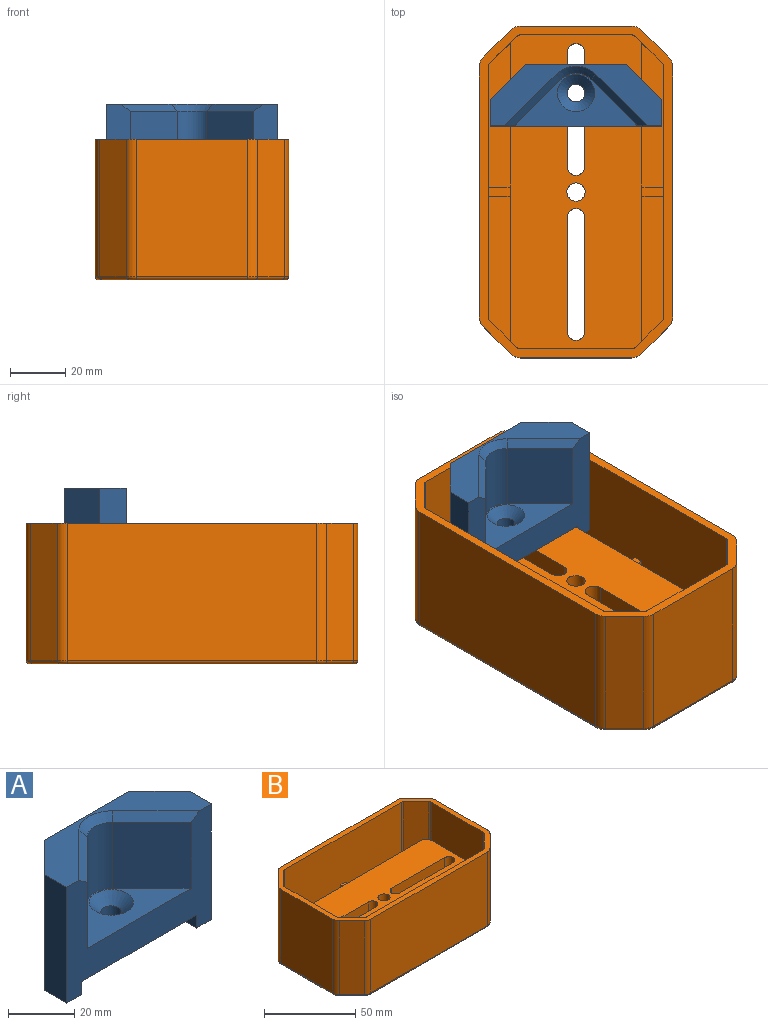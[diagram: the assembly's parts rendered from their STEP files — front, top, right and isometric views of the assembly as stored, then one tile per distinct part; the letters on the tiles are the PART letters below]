
ASSEMBLY  parts=2 mates=1
PART A: 21 faces, bbox 61.9x22.2x42.9 mm
  f0: plane 61.91x42.86mm, normal (0,-1,0), area 1210.6mm2, adj f1,f2,f5,f6,f7,f9,f10,f11
  f1: plane 61.91x22.23mm, normal (0,0,1), area 570.5mm2, adj f0,f3,f4,f5,f7,f8,f16,f17
  f2: plane 15.88x6.35mm, normal (0,0,-1), area 80.6mm2, adj f0,f7,f8,f10
  f3: plane 38.1x36.51mm, normal (0,1,0), area 1391.1mm2, adj f1,f4,f8,f11
  f4: plane 42.86x12.7mm, normal (-0.71,0.71,0), area 727.1mm2, adj f1,f3,f5,f6,f9,f11
  f5: plane 42.86x9.53mm, normal (-1,0,0), area 408.3mm2, adj f0,f1,f4,f6
  f6: plane 15.88x6.35mm, normal (0,0,-1), area 80.6mm2, adj f0,f4,f5,f9
  f7: plane 42.86x9.53mm, normal (1,0,0), area 408.3mm2, adj f0,f1,f2,f8
  f8: plane 42.86x12.7mm, normal (0.71,0.71,0), area 727.1mm2, adj f1,f2,f3,f7,f10,f11
  f9: plane 15.88x4.76mm, normal (1,0,0), area 75.6mm2, adj f0,f4,f6,f11
  f10: plane 15.88x4.76mm, normal (-1,0,0), area 75.6mm2, adj f0,f2,f8,f11
  f11: plane 49.21x22.23mm, normal (0,0,-1), area 1021.3mm2, adj f0,f3,f4,f8,f9,f10,f19
  f12: plane 24.45x16.81mm, normal (0.71,-0.71,0), area 581mm2, adj f0,f14,f15,f16
  f13: plane 24.45x16.81mm, normal (-0.71,-0.71,0), area 581mm2, adj f0,f14,f15,f18
  f14: cylinder r=7.67mm len=24.45mm, axis (0,0,1), area 294.4mm2, adj f12,f13,f15,f17
  f15: plane 44.45x19.05mm, normal (0,0,1), area 339.5mm2, adj f0,f12,f13,f14,f20
  f16: plane 20.4x18.6mm, normal (0.5,-0.5,0.71), area 89.9mm2, adj f0,f1,f12,f17
  f17: cone r=7.67mm half-angle=45deg, axis (0,0,1), area 50.4mm2, adj f1,f14,f16,f18
  f18: plane 20.4x18.6mm, normal (-0.5,-0.5,0.71), area 89.9mm2, adj f0,f1,f13,f17
  f19: cylinder r=3.2mm len=7.59mm, axis (0,0,1), area 152.7mm2, adj f11,f20
  f20: cone r=3.2mm half-angle=45deg, axis (0,0,1), area 155.1mm2, adj f15,f19
PART B: 81 faces, bbox 120.7x70.7x50.8 mm
  f0: plane 113.54x47.63mm, normal (0,0,1), area 4768.3mm2, adj f18,f20,f22,f23,f24,f25,f28,f29
  f1: plane 49.53x40.24mm, normal (-1,0,0), area 1993.2mm2, adj f5,f16,f17,f35
  f2: plane 90.28x49.53mm, normal (0,-1,0), area 4471.5mm2, adj f5,f10,f11,f42
  f3: plane 49.53x40.24mm, normal (1,0,0), area 1993.2mm2, adj f5,f12,f13,f50
  f4: plane 90.28x49.53mm, normal (0,1,0), area 4471.5mm2, adj f5,f14,f15,f43
  f5: plane 119.89x69.85mm, normal (0,0,1), area 1073.1mm2, adj f1,f2,f3,f4,f6,f7,f8,f9
  f6: plane 49.53x9.72mm, normal (-0.71,0.71,0), area 681.1mm2, adj f5,f14,f16,f39
  f7: plane 49.53x9.72mm, normal (0.71,0.71,0), area 681.1mm2, adj f5,f12,f15,f47
  f8: plane 49.53x9.72mm, normal (0.71,-0.71,0), area 681.1mm2, adj f5,f10,f13,f46
  f9: plane 49.53x9.72mm, normal (-0.71,-0.71,0), area 681.1mm2, adj f5,f11,f17,f38
  f10: cylinder r=5.08mm len=49.53mm, axis (0,0,1), area 197.6mm2, adj f2,f5,f8,f44
  f11: cylinder r=5.08mm len=49.53mm, axis (0,0,1), area 197.6mm2, adj f2,f5,f9,f40
  f12: cylinder r=5.08mm len=49.53mm, axis (0,0,-1), area 197.6mm2, adj f3,f5,f7,f49
  f13: cylinder r=5.08mm len=49.53mm, axis (0,0,-1), area 197.6mm2, adj f3,f5,f8,f48
  f14: cylinder r=5.08mm len=49.53mm, axis (0,0,-1), area 197.6mm2, adj f4,f5,f6,f41
  f15: cylinder r=5.08mm len=49.53mm, axis (0,0,-1), area 197.6mm2, adj f4,f5,f7,f45
  f16: cylinder r=5.08mm len=49.53mm, axis (0,0,1), area 197.6mm2, adj f1,f5,f6,f37
  f17: cylinder r=5.08mm len=49.53mm, axis (0,0,1), area 197.6mm2, adj f1,f5,f9,f36
  f18: plane 40.24x25.4mm, normal (1,0,0), area 1022.1mm2, adj f0,f5,f32,f33
  f19: plane 90.28x47.63mm, normal (0,1,0), area 4249.2mm2, adj f5,f26,f27,f74,f75,f76,f77,f79
  f20: plane 40.24x25.4mm, normal (-1,0,0), area 1022.1mm2, adj f0,f5,f28,f29
  f21: plane 90.28x47.63mm, normal (0,-1,0), area 4249.2mm2, adj f5,f30,f31,f69,f70,f71,f72,f80
  f22: plane 47.63x9.72mm, normal (0.71,-0.71,0), area 581.2mm2, adj f0,f5,f30,f32,f69,f73
  f23: plane 47.63x9.72mm, normal (-0.71,-0.71,0), area 581.2mm2, adj f0,f5,f28,f31,f71,f73
  f24: plane 47.63x9.72mm, normal (-0.71,0.71,0), area 581.2mm2, adj f0,f5,f26,f29,f74,f78
  f25: plane 47.63x9.72mm, normal (0.71,0.71,0), area 581.2mm2, adj f0,f5,f27,f33,f76,f78
  f26: cylinder r=1.91mm len=47.63mm, axis (0,0,1), area 71.3mm2, adj f5,f19,f24,f74
  f27: cylinder r=1.91mm len=47.63mm, axis (0,0,1), area 71.3mm2, adj f5,f19,f25,f76
  f28: cylinder r=1.91mm len=25.4mm, axis (0,0,-1), area 38mm2, adj f0,f5,f20,f23
  f29: cylinder r=1.91mm len=25.4mm, axis (0,0,-1), area 38mm2, adj f0,f5,f20,f24
  f30: cylinder r=1.91mm len=47.63mm, axis (0,0,-1), area 71.3mm2, adj f5,f21,f22,f69
  f31: cylinder r=1.91mm len=47.63mm, axis (0,0,-1), area 71.3mm2, adj f5,f21,f23,f71
  f32: cylinder r=1.91mm len=25.4mm, axis (0,0,1), area 38mm2, adj f0,f5,f18,f22
  f33: cylinder r=1.91mm len=25.4mm, axis (0,0,1), area 38mm2, adj f0,f5,f18,f25
  f34: plane 117.35x67.31mm, normal (0,0,-1), area 3293.2mm2, adj f35,f36,f37,f38,f39,f40,f41,f42
  f35: cylinder r=1.27mm len=40.24mm, axis (0,-1,0), area 80.3mm2, adj f1,f34,f36,f37
  f36: torus R=3.81mm, axis (0,0,1), area 7.2mm2, adj f17,f34,f35,f38
  f37: torus R=3.81mm, axis (0,0,1), area 7.2mm2, adj f16,f34,f35,f39
  f38: cylinder r=1.27mm len=10.62mm, axis (0.71,-0.71,0), area 27.4mm2, adj f9,f34,f36,f40
  f39: cylinder r=1.27mm len=10.62mm, axis (0.71,0.71,0), area 27.4mm2, adj f6,f34,f37,f41
  f40: torus R=3.81mm, axis (0,0,1), area 7.2mm2, adj f11,f34,f38,f42
  f41: torus R=3.81mm, axis (0,0,1), area 7.2mm2, adj f14,f34,f39,f43
  f42: cylinder r=1.27mm len=90.28mm, axis (1,0,0), area 180.1mm2, adj f2,f34,f40,f44
  f43: cylinder r=1.27mm len=90.28mm, axis (-1,0,0), area 180.1mm2, adj f4,f34,f41,f45
  f44: torus R=3.81mm, axis (0,0,1), area 7.2mm2, adj f10,f34,f42,f46
  f45: torus R=3.81mm, axis (0,0,1), area 7.2mm2, adj f15,f34,f43,f47
  f46: cylinder r=1.27mm len=10.62mm, axis (-0.71,-0.71,0), area 27.4mm2, adj f8,f34,f44,f48
  f47: cylinder r=1.27mm len=10.62mm, axis (-0.71,0.71,0), area 27.4mm2, adj f7,f34,f45,f49
  f48: torus R=3.81mm, axis (0,0,1), area 7.2mm2, adj f13,f34,f46,f50
  f49: torus R=3.81mm, axis (0,0,1), area 7.2mm2, adj f12,f34,f47,f50
  f50: cylinder r=1.27mm len=40.24mm, axis (0,1,0), area 80.3mm2, adj f3,f34,f48,f49
  f51: plane 31.75x12.7mm, normal (1,0,0), area 403.2mm2, adj f34,f52,f58,f59
  f52: cylinder r=3.17mm len=12.7mm, axis (0,0,-1), area 63.3mm2, adj f34,f51,f53,f59
  f53: plane 107.19x12.7mm, normal (0,-1,0), area 1361.3mm2, adj f34,f52,f54,f59
  f54: cylinder r=3.17mm len=12.7mm, axis (0,0,-1), area 63.3mm2, adj f34,f53,f55,f59
  f55: plane 31.75x12.7mm, normal (-1,0,0), area 403.2mm2, adj f34,f54,f56,f59
  f56: cylinder r=3.17mm len=12.7mm, axis (0,0,-1), area 63.3mm2, adj f34,f55,f57,f59
  f57: plane 107.19x12.7mm, normal (0,1,0), area 1361.3mm2, adj f34,f56,f58,f59
  f58: cylinder r=3.17mm len=12.7mm, axis (0,0,-1), area 63.3mm2, adj f34,f51,f57,f59
  f59: plane 113.54x38.1mm, normal (0,0,-1), area 3695.4mm2, adj f51,f52,f53,f54,f55,f56,f57,f58
  f60: cylinder r=3.3mm len=12.7mm, axis (0,0,1), area 263.3mm2, adj f0,f59
  f61: plane 41.28x12.7mm, normal (0,-1,0), area 524.2mm2, adj f0,f59,f62,f64
  f62: cylinder r=3.17mm len=12.7mm, axis (0,0,1), area 126.7mm2, adj f0,f59,f61,f63
  f63: plane 41.28x12.7mm, normal (0,1,0), area 524.2mm2, adj f0,f59,f62,f64
  f64: cylinder r=3.17mm len=12.7mm, axis (0,0,1), area 126.7mm2, adj f0,f59,f61,f63
  f65: plane 41.28x12.7mm, normal (0,-1,0), area 524.2mm2, adj f0,f59,f66,f68
  f66: cylinder r=3.17mm len=12.7mm, axis (0,0,1), area 126.7mm2, adj f0,f59,f65,f67
  f67: plane 41.28x12.7mm, normal (0,1,0), area 524.2mm2, adj f0,f59,f66,f68
  f68: cylinder r=3.17mm len=12.7mm, axis (0,0,1), area 126.7mm2, adj f0,f59,f65,f67
  f69: plane 52.28x7.94mm, normal (0,0,1), area 383.4mm2, adj f21,f22,f30,f70,f73
  f70: plane 15.88x7.94mm, normal (-1,0,0), area 126mm2, adj f21,f69,f73,f80
  f71: plane 52.28x7.94mm, normal (0,0,1), area 383.4mm2, adj f21,f23,f31,f72,f73
  f72: plane 15.88x7.94mm, normal (1,0,0), area 126mm2, adj f21,f71,f73,f80
  f73: plane 107.73x22.23mm, normal (0,1,0), area 2344mm2, adj f0,f22,f23,f69,f70,f71,f72,f80
  f74: plane 52.28x7.94mm, normal (0,0,1), area 383.4mm2, adj f19,f24,f26,f75,f78
  f75: plane 15.88x7.94mm, normal (1,0,0), area 126mm2, adj f19,f74,f78,f79
  f76: plane 52.28x7.94mm, normal (0,0,1), area 383.4mm2, adj f19,f25,f27,f77,f78
  f77: plane 15.88x7.94mm, normal (-1,0,0), area 126mm2, adj f19,f76,f78,f79
  f78: plane 107.73x22.23mm, normal (0,-1,0), area 2344mm2, adj f0,f24,f25,f74,f75,f76,f77,f79
  f79: plane 7.94x3.18mm, normal (0,0,1), area 25.2mm2, adj f19,f75,f77,f78
  f80: plane 7.94x3.18mm, normal (0,0,1), area 25.2mm2, adj f21,f70,f72,f73
PLACE A t=(78.01,146.85,37.22)mm
PLACE B rot(axis=(0,0,-1),90deg) t=(74.04,160.75,38.8)mm
MATE pin_slot B.f0 <-> A.f19  axis (0,0,1) through (108.97,130.59,41.98)mm
